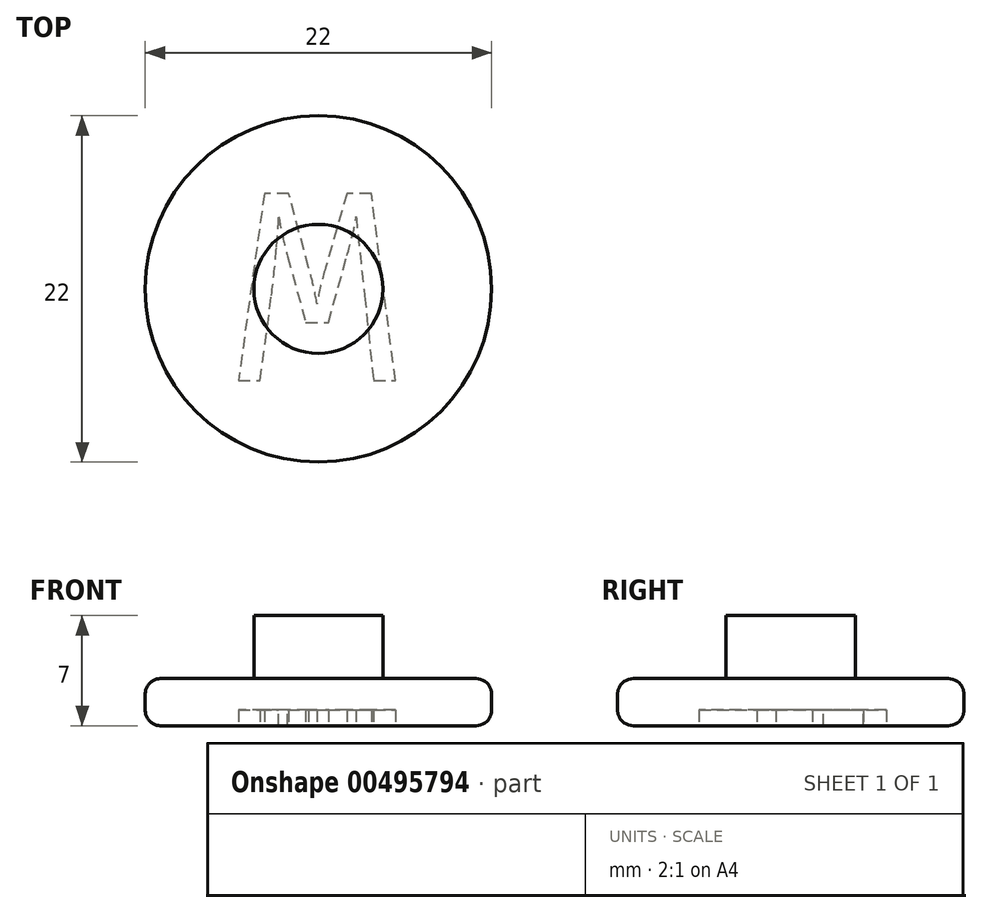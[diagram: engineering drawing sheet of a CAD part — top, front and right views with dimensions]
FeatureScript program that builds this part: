
annotation { "Feature Type Name" : "Feature", "Feature Type Description" : "" }
export const myFeature = defineFeature(function(context is Context, id is Id, definition is map)
    precondition{}
    {
        {
            var Q0;
            Q0=qCreatedBy(makeId("Front.planeOp"),FACE);
            var sketch = newSketch(context, id + "F0", { "sketchPlane" : qUnion([Q0])});
            skLineSegment(sketch, "E0.bottom", {"start": v(0, 0) * mm, "end": v(4.1, 0) * mm});
            skLineSegment(sketch, "E0.top", {"start": v(0, 4) * mm, "end": v(4.1, 4) * mm});
            skLineSegment(sketch, "E0.left", {"start": v(0, 0) * mm, "end": v(0, 4) * mm});
            skLineSegment(sketch, "E0.right", {"start": v(4.1, 0) * mm, "end": v(4.1, 4) * mm});
            skLineSegment(sketch, "E1.bottom", {"start": v(4.1, 0) * mm, "end": v(-6.9, 0) * mm});
            skLineSegment(sketch, "E1.top", {"start": v(4.1, -3) * mm, "end": v(-6.9, -3) * mm});
            skLineSegment(sketch, "E1.left", {"start": v(4.1, 0) * mm, "end": v(4.1, -3) * mm});
            skLineSegment(sketch, "E1.right", {"start": v(-6.9, 0) * mm, "end": v(-6.9, -3) * mm});
            skSolve(sketch);
        }
        {
            var Q0;
            Q0=makeQuery(id+"F0.imprint","IMPRINT",FACE,{"disambiguationData":[TD([[makeQuery(id+"F0.imprint","IMPRINT",EDGE,{"derivedFrom":sQuery(id+"F0.wireOp",EDGE,"E0.top")}),-1.0]])]});
            var Q1;
            Q1=makeQuery(id+"F0.imprint","IMPRINT",FACE,{"disambiguationData":[TD([[makeQuery(id+"F0.imprint","IMPRINT",EDGE,{"derivedFrom":sQuery(id+"F0.wireOp",EDGE,"E1.top")}),-1.0]])]});
            var Q2;
            Q2=sQuery(id+"F0.wireOp",EDGE,"E0.right");
            revolve(context, id + "F1", {"entities" : qUnion([Q0, Q1]), "axis" : qUnion([Q2]), "revolveType" : RevolveType.FULL});
        }
        {
            var Q0;
            Q0=makeQuery(id+"F1.opRevolve","SWEPT_EDGE",EDGE,{"disambiguationData":[OSD([sQuery(id+"F0.wireOp",EDGE,"E1.top"),sQuery(id+"F0.wireOp",EDGE,"E1.right")])]});
            var Q1;
            Q1=makeQuery(id+"F1.opRevolve","SWEPT_EDGE",EDGE,{"disambiguationData":[OSD([sQuery(id+"F0.wireOp",EDGE,"E1.bottom"),sQuery(id+"F0.wireOp",EDGE,"E1.right")])]});
            fillet(context, id + "F2", {"entities" : qUnion([Q0, Q1]), "radius" : 1 * mm, "tangentPropagation" : true, "allowEdgeOverflow" : false});
        }
        {
            var Q0;
            Q0=makeQuery(id+"F1.opRevolve","SWEPT_FACE",FACE,{"disambiguationData":[OSD([sQuery(id+"F0.wireOp",EDGE,"E1.top")])]});
            var sketch = newSketch(context, id + "F3", { "sketchPlane" : qUnion([Q0])});
            skText(sketch, "E2", { "text": "W", "fontName": "DroidSansMono.ttf"});
            const initialGuessF3  = {"E2": [-0.001, -0.00607, 1, 0, 0.012]};
            skSetInitialGuess(sketch, initialGuessF3);
            skSolve(sketch);
        }
        {
            var Q0;
            Q0 = qSketchRegion(id + "F3", true);
            extrude(context, id + "F4", {"entities" : qUnion([Q0]), "operationType" : NewBodyOperationType.REMOVE, "oppositeDirection" : true, "depth" : 1 * mm});
        }
    });
